# Revit family: cRoller_Blind-Decor_Systems-Blindset
name_source: partatom
category: Specialty Equipment
units: mm (PartAtom-declared; Revit-internal decimal feet)

## family parameters
Always vertical = Yes
Cut with Voids When Loaded = No
OmniClass Number = 23.40.95.11.31
OmniClass Title = Movable or Retractable Screens
Part Type = Normal
Room Calculation Point = No
Round Connector Dimension = Use Diameter
Shared = No
Work Plane-Based = No

## types (6) — shared parameters
Assembly Code = E1090900
Blind Finish = Fabric - Decor Systems - Custom Color
Blind Finish Note = Custom RGB Values can be changed in the Material for the "Blind Finish"
C Curtain Side Offset = 0' - 0 25/32"
Default Elevation = 0' - 0"
Description = Pre-installed modular roller blind
Keynote = 12490
Manufacturer = Decor Systems
Model = BlindSet
Product Documentation Link = https://blindset.co.uk
Product Page URL = https://blindset.co.uk
Profile Finish = Metal - Decor Systems - White Powdercoat
URL = https://www.decorsystems.co.uk
Version = 2020 - v1.0a
Video Link = https://blindset.co.uk

## per-type parameters (varying)
| type | Constraints |
| Box and Closure | 1 |
| Box and Closure with additional drylining transition | 2 |
| Box and Closure with additional plain transition | 3 |
| Box and Closure with Integrated Curtain Track | 4 |
| Box and Closure with Integrated curtain track and additional drylining transition | 5 |
| Box and Closure with Integrated curtain track and additional plain transition | 6 |

## geometry (parser evidence)
native form markers: Extrusion x6, Sweep x7
no freeform markers — native parametric forms only
